# Revit family: Motus Pendant 180 BL 700 DALI 830 C2_Unhosted
name_source: partatom
category: Lighting Fixtures
revit_build: Autodesk Revit 2016 (Build: 20151007_0715(x64)
units: mm (PartAtom-declared; Revit-internal decimal feet)

## family parameters
Always vertical = Yes
Cut with Voids When Loaded = No
Light Source = Yes
OmniClass Number = 23.80.70.00
OmniClass Title = Lighting
Part Type = Normal
Room Calculation Point = No
Round Connector Dimension = Use Diameter
Shared = No
Work Plane-Based = No

## types (1)
- Motus Pendant 180 BL 700 DALI 830 C2_Unhosted
    Apparent Load = 7 VA
    ArticleNumber = MOT536695
    Body Material and Colour = <By Category>
    Color Filter = 16777215
    Decor visible = Yes
    Description = Motus Pendant 180 BL 700 DALI 830 C2
    Diameter = 180 mm  [stored 0.590551 ft]
    Dimming Lamp Color Temperature Shift = <None>
    DistanceFromCeiling = 900 mm  [stored 2.95276 ft]
    EANNo = 4741145366953
    Emit Shape Visible in Rendering = Yes
    Emit from Circle Diameter = 165 mm  [stored 0.541339 ft]
    Expired = 0
    Frequency = 50 Hz
    FrequencyMax = 60 Hz
    Glamox Category = Architectural
    Glamox Family = Motus Pendant
    Glamox Metal = Glamox Metal
    Glamox Mounting = Pendant
    GlobalTradeItemNumber = 4741145366953
    Height = 100 mm  [stored 0.328084 ft]
    IFC Classification = Light Fixture
    IPClass = 20
    IP_Code = 20
    Lamp = LED
    LightFixtureMountingType = SUSPENDED
    LightFixturePlacingType = CEILING
    LumDiameter = 180 mm  [stored 0.590551 ft]
    MFArtNo = MOT536695
    MaintenanceFactor = 0
    Manufacturer = Glamox
    Maximum TA = 25
    Model = A50 57HF TC-TEL
    ModelLabel = Motus Pendant 180 BL 700 DALI 830 C2
    ModelReference = Motus Pendant
    NominalFrequencyRange = 50 Hz
    Number of Poles = 1
    Photometric Web File = MOTUS-PENDANT-180-700-830.ies
    Power Factor = 0.98
    PowerFactor = 98.00%
    Radius = 90 mm  [stored 0.295276 ft]
    Radius1 = 75 mm
    RatedVoltage = 100 V
    Specification = Architectural luminaries, for Pendant mounting, circular with diameter 180mm, IP20, light source LED, lumen out 648lm, ballast type DALI.
    Tilt Angle = 90.00°
    Total Load = 7 W
    TotalWattage = 7 W
    TypeOfBallast = DALI
    URL Denmark = http://glamox.com
    URL Estonia = http://glamox.com
    URL Finland = http://glamox.com
    URL Germany = http://glamox.com
    URL Ireland = http://glamox.com
    URL Norway = http://glamox.com
    URL Other = http://glamox.com
    URL Russia = http://glamox.com
    URL Sweden = http://glamox.com
    URL UK = http://glamox.com
    UpdateDate = 02.03.2021 13:22:52
    Voltage = 100 V
    VoltageMax = 240 V

note: [stored X ft] marks values corroborated as IEEE doubles in the binary element streams (Revit-internal decimal feet)

## geometry (parser evidence)
native form markers: Sweep x3
no freeform markers — native parametric forms only
